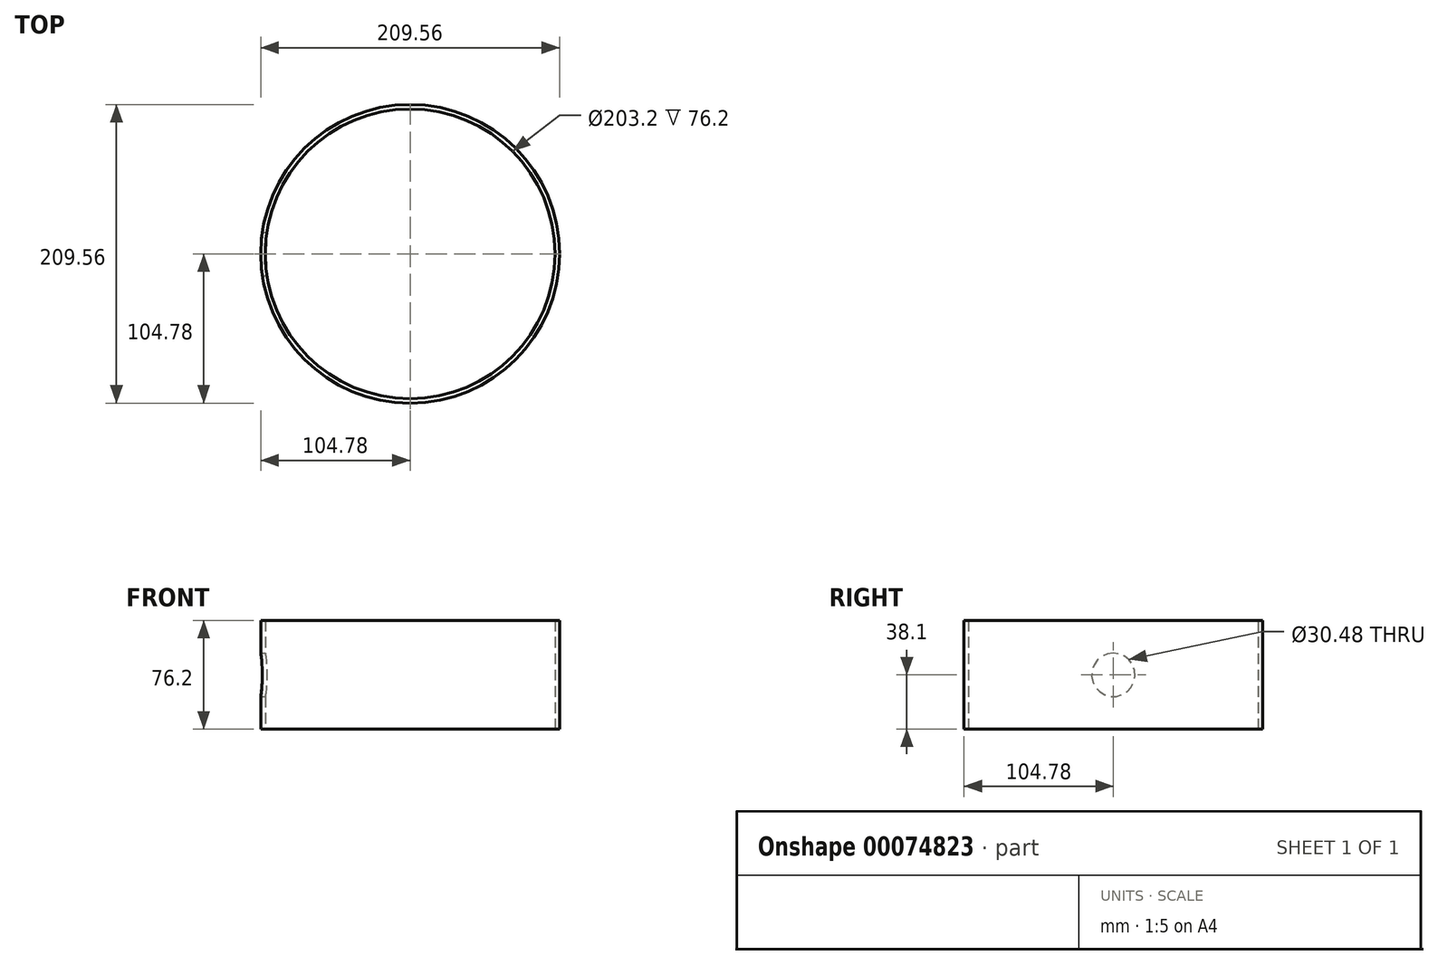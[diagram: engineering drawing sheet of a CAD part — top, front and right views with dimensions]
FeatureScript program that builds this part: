
annotation { "Feature Type Name" : "Feature", "Feature Type Description" : "" }
export const myFeature = defineFeature(function(context is Context, id is Id, definition is map)
    precondition{}
    {
        {
            var Q0;
            Q0=qCreatedBy(makeId("Top.planeOp"),FACE);
            var sketch = newSketch(context, id + "F0", { "sketchPlane" : qUnion([Q0])});
            skCircle(sketch, "E0", {"center": v(0, 0) * mm, "radius": 104.78 * mm});
            skCircle(sketch, "E1", {"center": v(0, 0) * mm, "radius": 101.6 * mm});
            skSolve(sketch);
        }
        {
            var Q0;
            Q0 = qSketchRegion(id + "F0", true);
            extrude(context, id + "F1", {"entities" : qUnion([Q0]), "endBound" : BoundingType.SYMMETRIC, "depth" : 76.2 * mm});
        }
        {
            var Q0;
            Q0=qCreatedBy(makeId("Right.planeOp"),FACE);
            var sketch = newSketch(context, id + "F2", { "sketchPlane" : qUnion([Q0])});
            skCircle(sketch, "E2", {"center": v(0, 0) * mm, "radius": 15.24 * mm});
            skSolve(sketch);
        }
        {
            var Q0;
            Q0 = qSketchRegion(id + "F2", true);
            extrude(context, id + "F3", {"entities" : qUnion([Q0]), "operationType" : NewBodyOperationType.REMOVE, "endBound" : BoundingType.THROUGH_ALL, "oppositeDirection" : true, "depth" : 25.4 * mm});
        }
    });
